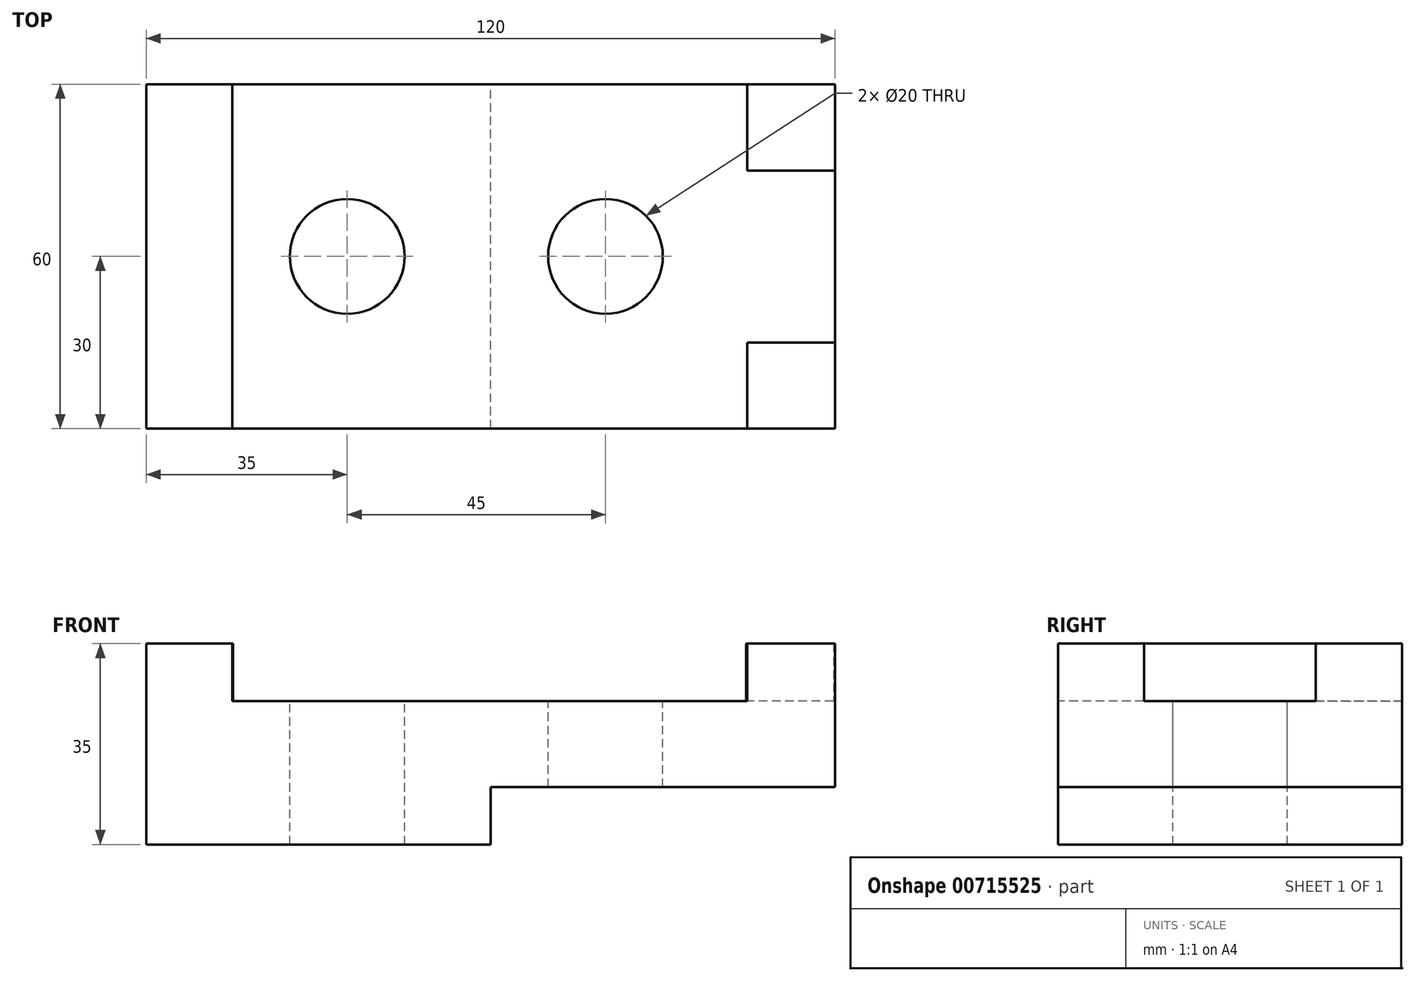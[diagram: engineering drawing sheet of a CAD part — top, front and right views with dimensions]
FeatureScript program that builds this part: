
annotation { "Feature Type Name" : "Feature", "Feature Type Description" : "" }
export const myFeature = defineFeature(function(context is Context, id is Id, definition is map)
    precondition{}
    {
        {
            var Q0;
            Q0=qCreatedBy(makeId("Top.planeOp"),FACE);
            var sketch = newSketch(context, id + "F0", { "sketchPlane" : qUnion([Q0])});
            skLineSegment(sketch, "E0.bottom", {"start": v(30, -30) * mm, "end": v(-30, -30) * mm});
            skLineSegment(sketch, "E0.top", {"start": v(30, 30) * mm, "end": v(-30, 30) * mm});
            skLineSegment(sketch, "E0.left", {"start": v(30, -30) * mm, "end": v(30, 30) * mm});
            skLineSegment(sketch, "E0.right", {"start": v(-30, -30) * mm, "end": v(-30, 30) * mm});
            skPoint(sketch, "E0.middle", {"position": v(0, 0) * mm});
            skSolve(sketch);
        }
        {
            var Q0;
            Q0 = qSketchRegion(id + "F0", true);
            extrude(context, id + "F1", {"entities" : qUnion([Q0]), "depth" : 10 * mm, "offsetDistance" : 25 * mm});
        }
        {
            var Q0;
            Q0=makeQuery(id+"F1.opExtrude","CAP_FACE",FACE,{"disambiguationData":[OSD([sQuery(id+"F0.wireOp",EDGE,"E0.bottom"),sQuery(id+"F0.wireOp",EDGE,"E0.top"),sQuery(id+"F0.wireOp",EDGE,"E0.left"),sQuery(id+"F0.wireOp",EDGE,"E0.right")])],"isStart":false});
            var sketch = newSketch(context, id + "F2", { "sketchPlane" : qUnion([Q0])});
            skLineSegment(sketch, "E1.bottom", {"start": v(-30, -30) * mm, "end": v(90, -30) * mm});
            skLineSegment(sketch, "E1.top", {"start": v(-30, 30) * mm, "end": v(90, 30) * mm});
            skLineSegment(sketch, "E1.left", {"start": v(-30, -30) * mm, "end": v(-30, 30) * mm});
            skLineSegment(sketch, "E1.right", {"start": v(90, -30) * mm, "end": v(90, 30) * mm});
            skSolve(sketch);
        }
        {
            var Q0;
            {var subQ2=sQuery(id+"F2.wireOp",EDGE,"E1.left");Q0=makeQuery(id+"F2.imprint","IMPRINT",FACE,{"disambiguationData":[TD([[makeQuery(id+"F2.imprint","IMPRINT",EDGE,{"derivedFrom":subQ2}),-1.0]])]});}
            var Q1;
            {var subQ2=sQuery(id+"F2.wireOp",EDGE,"E1.right");Q1=makeQuery(id+"F2.imprint","IMPRINT",FACE,{"disambiguationData":[TD([[makeQuery(id+"F2.imprint","IMPRINT",EDGE,{"derivedFrom":subQ2}),1.0]])]});}
            extrude(context, id + "F3", {"entities" : qUnion([Q0, Q1]), "operationType" : NewBodyOperationType.ADD, "depth" : 25 * mm, "offsetDistance" : 25 * mm});
        }
        {
            var Q0;
            Q0=makeQuery(id+"F3.opExtrude","CAP_FACE",FACE,{"disambiguationData":[OSD([sQuery(id+"F2.wireOp",EDGE,"E1.bottom"),sQuery(id+"F2.wireOp",EDGE,"E1.top"),sQuery(id+"F2.wireOp",EDGE,"E1.left"),sQuery(id+"F2.wireOp",EDGE,"E1.right")])],"isStart":false});
            var sketch = newSketch(context, id + "F4", { "sketchPlane" : qUnion([Q0])});
            skLineSegment(sketch, "E2", {"start": v(-30, 30) * mm, "end": v(-15, 30) * mm});
            skLineSegment(sketch, "E3", {"start": v(-15, 30) * mm, "end": v(5, 30) * mm});
            skLineSegment(sketch, "E4", {"start": v(5, 30) * mm, "end": v(50, 30) * mm});
            skLineSegment(sketch, "E5", {"start": v(5, 30) * mm, "end": v(5, 0) * mm});
            skLineSegment(sketch, "E6", {"start": v(50, 30) * mm, "end": v(50, 0) * mm});
            skCircle(sketch, "E7", {"center": v(5, 0) * mm, "radius": 10 * mm});
            skCircle(sketch, "E8", {"center": v(50, 0) * mm, "radius": 10 * mm});
            skSolve(sketch);
        }
        {
            var Q0;
            Q0 = qSketchRegion(id + "F4", true);
            extrude(context, id + "F5", {"entities" : qUnion([Q0]), "operationType" : NewBodyOperationType.REMOVE, "oppositeDirection" : true, "depth" : 51.5 * mm, "offsetDistance" : 25 * mm});
        }
        {
            var Q0;
            Q0=makeQuery(id+"F4.imprint","IMPRINT",FACE,{"disambiguationData":[TD([[makeQuery(id+"F4.imprint","IMPRINT",EDGE,{"derivedFrom":sQuery(id+"F4.wireOp",EDGE,"E2")}),1.0]])]});
            var sketch = newSketch(context, id + "F6", { "sketchPlane" : qUnion([Q0])});
            skLineSegment(sketch, "E9", {"start": v(-30.02, 29.95) * mm, "end": v(-15.02, 29.95) * mm});
            skLineSegment(sketch, "E10", {"start": v(-15.02, 29.95) * mm, "end": v(-15.02, -30.05) * mm});
            skLineSegment(sketch, "E11", {"start": v(89.72, -30.05) * mm, "end": v(89.72, -15.05) * mm});
            skLineSegment(sketch, "E12", {"start": v(89.72, -15.05) * mm, "end": v(89.72, 14.95) * mm});
            skLineSegment(sketch, "E13", {"start": v(89.72, 14.95) * mm, "end": v(89.72, 29.95) * mm});
            skLineSegment(sketch, "E14", {"start": v(89.72, -15.05) * mm, "end": v(74.72, -15.05) * mm});
            skLineSegment(sketch, "E15", {"start": v(74.72, -15.05) * mm, "end": v(74.72, -30.05) * mm});
            skLineSegment(sketch, "E16", {"start": v(74.72, -30.05) * mm, "end": v(89.72, -30.05) * mm});
            skLineSegment(sketch, "E17", {"start": v(89.72, 14.95) * mm, "end": v(74.72, 14.95) * mm});
            skLineSegment(sketch, "E18", {"start": v(74.72, 14.95) * mm, "end": v(74.72, 29.95) * mm});
            skLineSegment(sketch, "E19", {"start": v(74.72, 29.95) * mm, "end": v(89.72, 29.95) * mm});
            skLineSegment(sketch, "E20", {"start": v(-15.02, 29.95) * mm, "end": v(74.72, 29.95) * mm});
            skLineSegment(sketch, "E21", {"start": v(-15.02, -30.05) * mm, "end": v(74.72, -30.05) * mm});
            skLineSegment(sketch, "E22", {"start": v(-15.02, -30.05) * mm, "end": v(-30, -30.05) * mm});
            skLineSegment(sketch, "E23", {"start": v(-30, -30.05) * mm, "end": v(-30.02, 29.95) * mm});
            skSolve(sketch);
        }
        {
            var Q0;
            Q0=makeQuery(id+"F6.imprint","IMPRINT",FACE,{"disambiguationData":[TD([[makeQuery(id+"F6.imprint","IMPRINT",EDGE,{"derivedFrom":sQuery(id+"F6.wireOp",EDGE,"E12")}),1.0]])]});
            extrude(context, id + "F7", {"entities" : qUnion([Q0]), "operationType" : NewBodyOperationType.REMOVE, "oppositeDirection" : true, "depth" : 10 * mm, "offsetDistance" : 25 * mm});
        }
        {
            var Q0;
            Q0=makeQuery(id+"F4.imprint","IMPRINT",FACE,{"disambiguationData":[TD([[makeQuery(id+"F4.imprint","IMPRINT",EDGE,{"derivedFrom":sQuery(id+"F4.wireOp",EDGE,"E2")}),1.0]])]});
            var sketch = newSketch(context, id + "F8", { "sketchPlane" : qUnion([Q0])});
            skLineSegment(sketch, "E24.bottom", {"start": v(-14.9, 30.23) * mm, "end": v(74.51, 30.23) * mm});
            skLineSegment(sketch, "E24.top", {"start": v(-14.9, 28.26) * mm, "end": v(74.51, 28.26) * mm});
            skLineSegment(sketch, "E24.left", {"start": v(-14.9, 30.23) * mm, "end": v(-14.9, 28.26) * mm});
            skLineSegment(sketch, "E24.right", {"start": v(74.51, 30.23) * mm, "end": v(74.51, 28.26) * mm});
            skSolve(sketch);
        }
        {
            var Q0;
            {var subQ3=sQuery(id+"F8.wireOp",EDGE,"E24.top");Q0=makeQuery(id+"F8.imprint","IMPRINT",FACE,{"disambiguationData":[TD([[makeQuery(id+"F8.imprint","IMPRINT",EDGE,{"derivedFrom":subQ3}),1.0]])]});}
            extrude(context, id + "F9", {"entities" : qUnion([Q0]), "operationType" : NewBodyOperationType.REMOVE, "oppositeDirection" : true, "depth" : 10 * mm, "offsetDistance" : 25 * mm});
        }
        {
            var Q0;
            Q0=makeQuery(id+"F4.imprint","IMPRINT",FACE,{"disambiguationData":[TD([[makeQuery(id+"F4.imprint","IMPRINT",EDGE,{"derivedFrom":sQuery(id+"F4.wireOp",EDGE,"E2")}),1.0]])]});
            var sketch = newSketch(context, id + "F10", { "sketchPlane" : qUnion([Q0])});
            skLineSegment(sketch, "E25.bottom", {"start": v(89.63, -15) * mm, "end": v(92.6, -15) * mm});
            skLineSegment(sketch, "E25.top", {"start": v(89.63, 14.92) * mm, "end": v(92.6, 14.92) * mm});
            skLineSegment(sketch, "E25.left", {"start": v(89.63, -15) * mm, "end": v(89.63, 14.92) * mm});
            skLineSegment(sketch, "E25.right", {"start": v(92.6, -15) * mm, "end": v(92.6, 14.92) * mm});
            skSolve(sketch);
        }
        {
            var Q0;
            Q0 = qSketchRegion(id + "F10", true);
            extrude(context, id + "F11", {"entities" : qUnion([Q0]), "operationType" : NewBodyOperationType.REMOVE, "oppositeDirection" : true, "depth" : 10 * mm, "offsetDistance" : 25 * mm});
        }
    });
